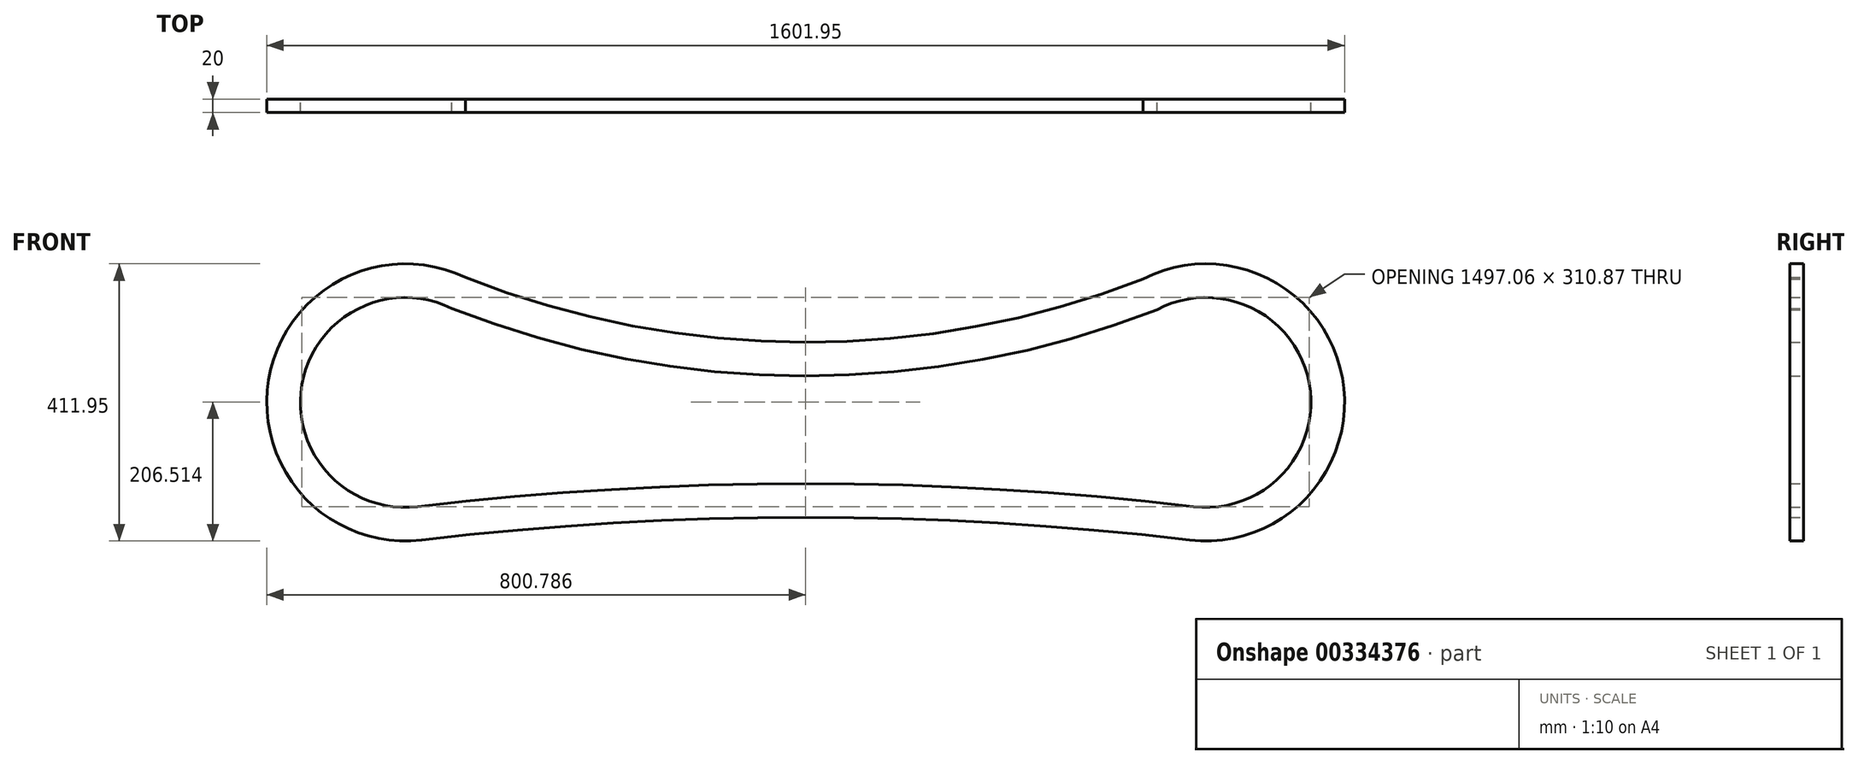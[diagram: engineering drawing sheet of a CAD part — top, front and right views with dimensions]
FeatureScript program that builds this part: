
annotation { "Feature Type Name" : "Feature", "Feature Type Description" : "" }
export const myFeature = defineFeature(function(context is Context, id is Id, definition is map)
    precondition{}
    {
        {
            var Q0;
            Q0=qCreatedBy(makeId("Front.planeOp"),FACE);
            var sketch = newSketch(context, id + "F0", { "sketchPlane" : qUnion([Q0])});
            skArc(sketch, "E0", {"start": v(-506.4, 187.38) * mm, "mid": v(-798.76, 35.51) * mm, "end": v(-571.33, -202.84) * mm});
            skArc(sketch, "E1", {"start": v(570.19, -202.84) * mm, "mid": v(797.2, 37.91) * mm, "end": v(500.9, 185.22) * mm});
            skLineSegment(sketch, "E2", {"start": v(-595.57, 1.7) * mm, "end": v(-0.57, 1.7) * mm});
            skArc(sketch, "E3", {"start": v(570.19, -202.84) * mm, "mid": v(-0.57, -169.14) * mm, "end": v(-571.33, -202.84) * mm});
            skPoint(sketch, "E3.centerSnap0", {"position": v(-0.57, 1.7) * mm});
            skArc(sketch, "E4", {"start": v(-506.4, 187.38) * mm, "mid": v(-2.96, 91.1) * mm, "end": v(500.9, 185.22) * mm});
            skArc(sketch, "E5.0", {"start": v(-526.56, 141.58) * mm, "mid": v(-2.69, 41.1) * mm, "end": v(521.55, 139.6) * mm});
            skArc(sketch, "E5.1", {"start": v(-526.56, 141.58) * mm, "mid": v(-749.3, 28.12) * mm, "end": v(-577.22, -153.19) * mm});
            skArc(sketch, "E5.2", {"start": v(576.07, -153.19) * mm, "mid": v(-0.57, -119.14) * mm, "end": v(-577.22, -153.19) * mm});
            skArc(sketch, "E5.3", {"start": v(576.07, -153.19) * mm, "mid": v(747.77, 30.26) * mm, "end": v(521.55, 139.6) * mm});
            skSolve(sketch);
        }
        {
            var Q0;
            Q0=makeQuery(id+"F0.imprint","IMPRINT",FACE,{"disambiguationData":[TD([[makeQuery(id+"F0.imprint","IMPRINT",EDGE,{"derivedFrom":sQuery(id+"F0.wireOp",EDGE,"E0")}),1.0]])]});
            extrude(context, id + "F1", {"entities" : qUnion([Q0]), "depth" : 20 * mm});
        }
    });
